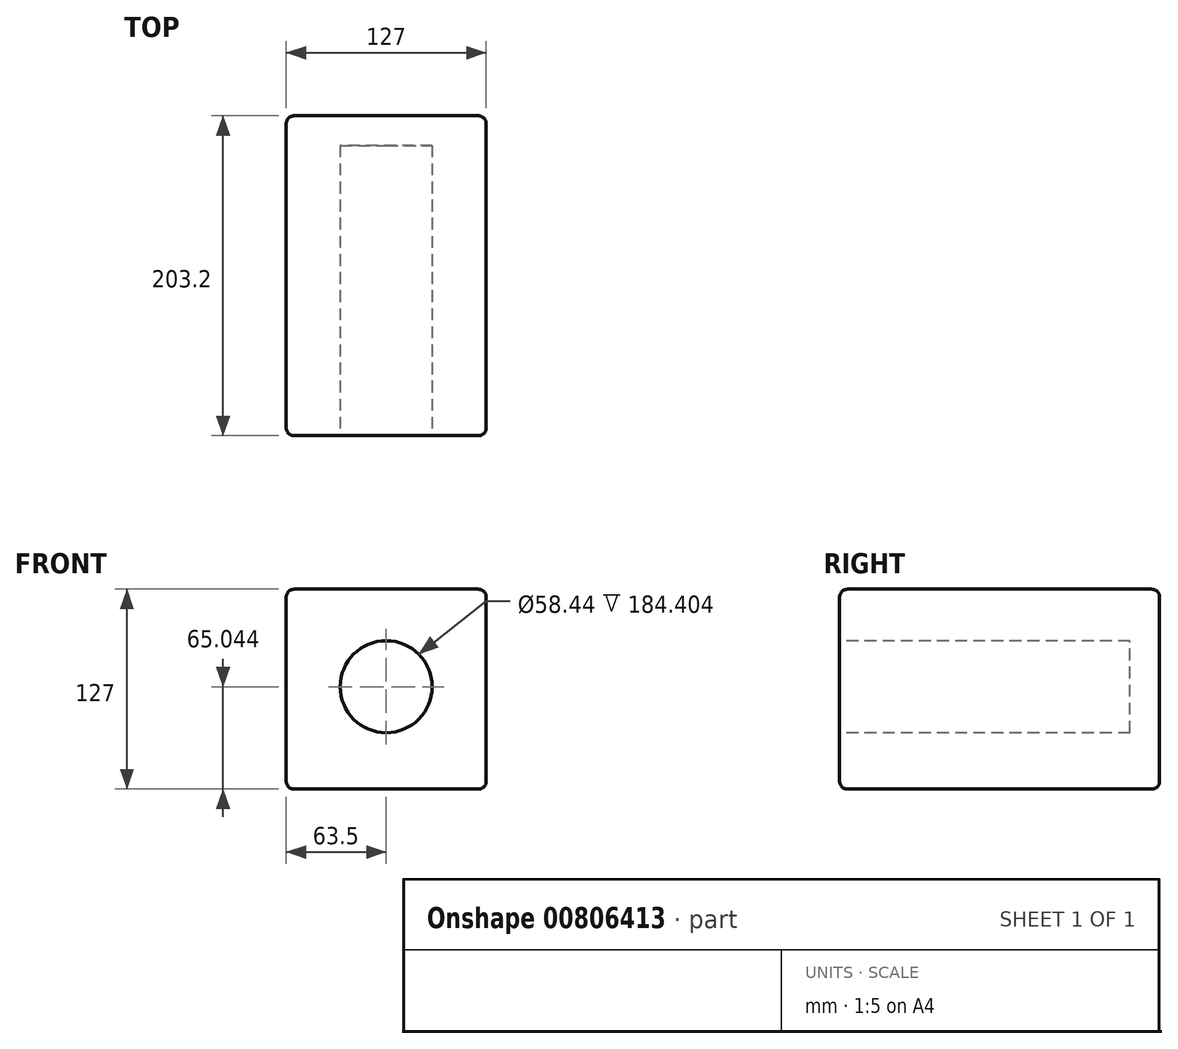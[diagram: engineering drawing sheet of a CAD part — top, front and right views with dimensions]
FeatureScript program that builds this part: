
annotation { "Feature Type Name" : "Feature", "Feature Type Description" : "" }
export const myFeature = defineFeature(function(context is Context, id is Id, definition is map)
    precondition{}
    {
        {
            var Q0;
            Q0=qCreatedBy(makeId("Top.planeOp"),FACE);
            var sketch = newSketch(context, id + "F0", { "sketchPlane" : qUnion([Q0])});
            skLineSegment(sketch, "E0.bottom", {"start": v(-63.5, 101.6) * mm, "end": v(63.5, 101.6) * mm});
            skLineSegment(sketch, "E0.top", {"start": v(-63.5, -101.6) * mm, "end": v(63.5, -101.6) * mm});
            skLineSegment(sketch, "E0.left", {"start": v(-63.5, 101.6) * mm, "end": v(-63.5, -101.6) * mm});
            skLineSegment(sketch, "E0.right", {"start": v(63.5, 101.6) * mm, "end": v(63.5, -101.6) * mm});
            skPoint(sketch, "E0.middle", {"position": v(0, 0) * mm});
            skSolve(sketch);
        }
        {
            var Q0;
            Q0=makeQuery(id+"F0.imprint","IMPRINT",FACE,{"disambiguationData":[TD([[makeQuery(id+"F0.imprint","IMPRINT",EDGE,{"derivedFrom":sQuery(id+"F0.wireOp",EDGE,"E0.bottom")}),-1.0]])]});
            extrude(context, id + "F1", {"entities" : qUnion([Q0]), "depth" : 127 * mm, "offsetDistance" : 25.4 * mm});
        }
        {
            var Q0;
            Q0=makeQuery(id+"F1.opExtrude","CAP_FACE",FACE,{"disambiguationData":[OSD([sQuery(id+"F0.wireOp",EDGE,"E0.bottom"),sQuery(id+"F0.wireOp",EDGE,"E0.top"),sQuery(id+"F0.wireOp",EDGE,"E0.left"),sQuery(id+"F0.wireOp",EDGE,"E0.right")])],"isStart":false});
            var Q1;
            Q1=makeQuery(id+"F1.opExtrude","SWEPT_FACE",FACE,{"disambiguationData":[OSD([sQuery(id+"F0.wireOp",EDGE,"E0.top")])]});
            var Q2;
            Q2=makeQuery(id+"F1.opExtrude","SWEPT_FACE",FACE,{"disambiguationData":[OSD([sQuery(id+"F0.wireOp",EDGE,"E0.right")])]});
            var Q3;
            Q3=makeQuery(id+"F1.opExtrude","SWEPT_FACE",FACE,{"disambiguationData":[OSD([sQuery(id+"F0.wireOp",EDGE,"E0.bottom")])]});
            var Q4;
            Q4=makeQuery(id+"F1.opExtrude","SWEPT_FACE",FACE,{"disambiguationData":[OSD([sQuery(id+"F0.wireOp",EDGE,"E0.left")])]});
            var Q5;
            Q5=makeQuery(id+"F1.opExtrude","CAP_FACE",FACE,{"disambiguationData":[OSD([sQuery(id+"F0.wireOp",EDGE,"E0.bottom"),sQuery(id+"F0.wireOp",EDGE,"E0.top"),sQuery(id+"F0.wireOp",EDGE,"E0.left"),sQuery(id+"F0.wireOp",EDGE,"E0.right")])],"isStart":true});
            fillet(context, id + "F2", {"entities" : qUnion([Q0, Q1, Q2, Q3, Q4, Q5]), "radius" : 5.08 * mm, "tangentPropagation" : true, "allowEdgeOverflow" : false});
        }
        {
            var Q0;
            Q0=makeQuery(id+"F1.opExtrude","SWEPT_FACE",FACE,{"disambiguationData":[OSD([sQuery(id+"F0.wireOp",EDGE,"E0.top")])]});
            var sketch = newSketch(context, id + "F3", { "sketchPlane" : qUnion([Q0])});
            skCircle(sketch, "E1", {"center": v(0, 65.04) * mm, "radius": 29.22 * mm});
            skSolve(sketch);
        }
        {
            var Q0;
            Q0=makeQuery(id+"F3.imprint","IMPRINT",FACE,{"disambiguationData":[TD([[makeQuery(id+"F3.imprint","IMPRINT",EDGE,{"derivedFrom":sQuery(id+"F3.wireOp",EDGE,"E1")}),1.0]])]});
            extrude(context, id + "F4", {"entities" : qUnion([Q0]), "operationType" : NewBodyOperationType.REMOVE, "oppositeDirection" : true, "depth" : 184.4 * mm, "offsetDistance" : 25.4 * mm});
        }
    });
